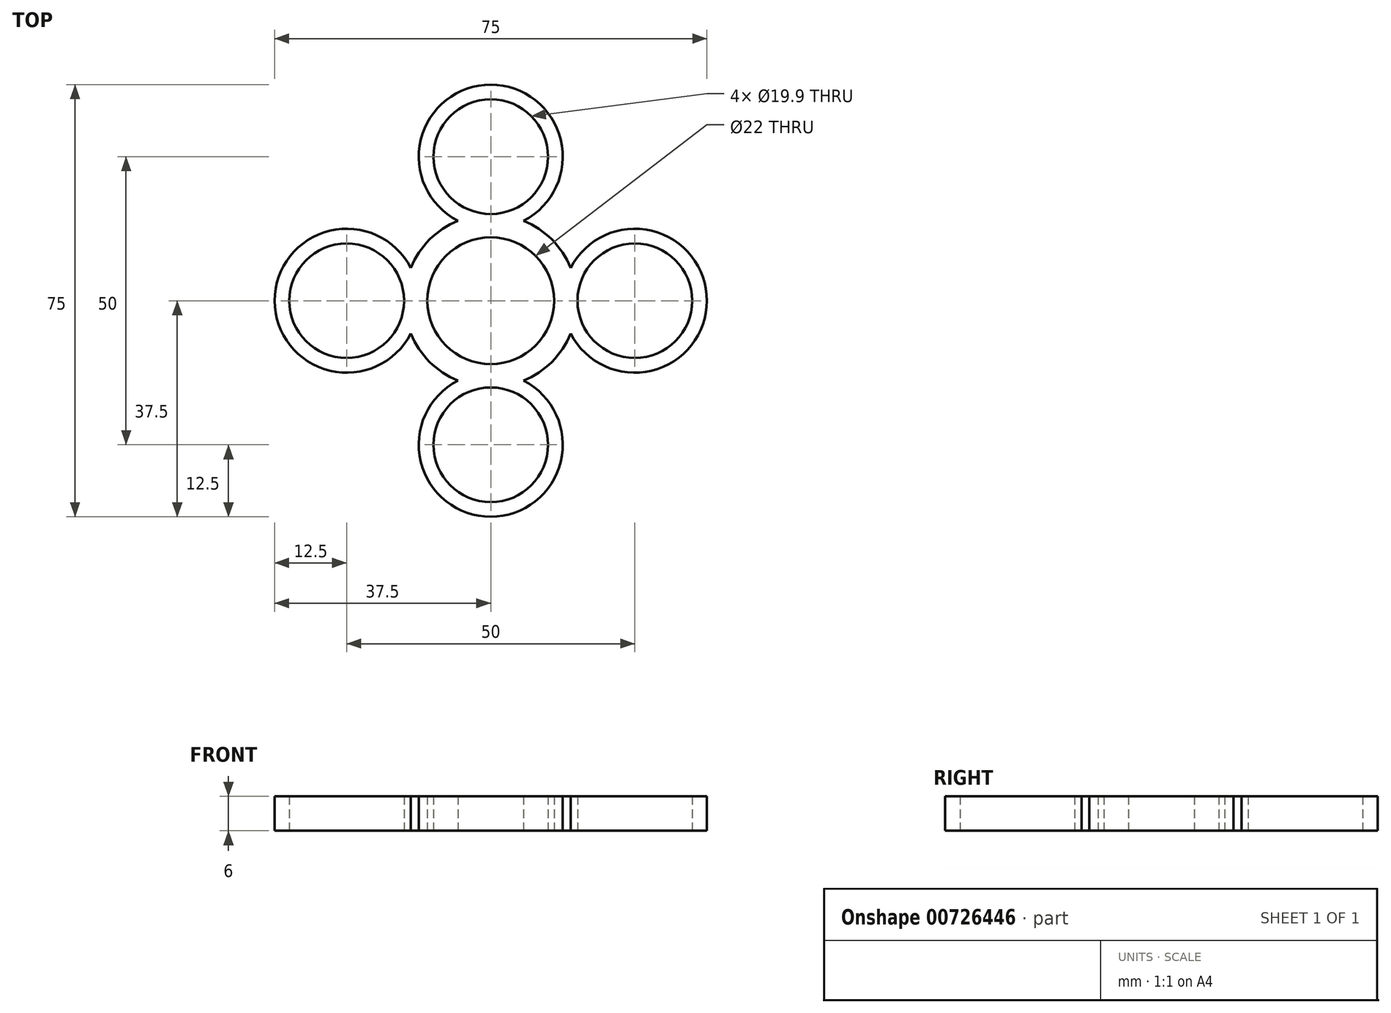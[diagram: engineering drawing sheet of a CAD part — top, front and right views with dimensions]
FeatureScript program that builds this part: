
annotation { "Feature Type Name" : "Feature", "Feature Type Description" : "" }
export const myFeature = defineFeature(function(context is Context, id is Id, definition is map)
    precondition{}
    {
        {
            var Q0;
            Q0=qCreatedBy(makeId("Top.planeOp"),FACE);
            var sketch = newSketch(context, id + "F0", { "sketchPlane" : qUnion([Q0])});
            skArc(sketch, "E0", {"start": v(11, 0) * mm, "mid": v(0, 11) * mm, "end": v(-11, 0) * mm});
            skCircle(sketch, "E1", {"center": v(0, 25) * mm, "radius": 9.95 * mm});
            skArc(sketch, "E2", {"start": v(-5.7, 13.87) * mm, "mid": v(-10.6, 10.6) * mm, "end": v(-13.87, 5.7) * mm});
            skArc(sketch, "E3", {"start": v(5.7, 13.88) * mm, "mid": v(0, 37.5) * mm, "end": v(-5.7, 13.88) * mm});
            skPoint(sketch, "E4.endSnap0", {"position": v(0, -15) * mm});
            skArc(sketch, "E5.trimOffspring", {"start": v(13.87, 5.7) * mm, "mid": v(10.6, 10.6) * mm, "end": v(5.7, 13.87) * mm});
            skPoint(sketch, "E4.end.orphan", {"position": v(0, -27.44) * mm});
            skCircle(sketch, "E6.1.0", {"center": v(-25, 0) * mm, "radius": 9.95 * mm});
            skArc(sketch, "E6.1.1", {"start": v(0, 11) * mm, "mid": v(-11, 0) * mm, "end": v(0, -11) * mm});
            skArc(sketch, "E6.1.2", {"start": v(-5.7, 13.87) * mm, "mid": v(-10.6, 10.6) * mm, "end": v(-13.88, 5.7) * mm});
            skArc(sketch, "E6.1.3", {"start": v(-13.87, -5.7) * mm, "mid": v(-10.6, -10.6) * mm, "end": v(-5.7, -13.87) * mm});
            skArc(sketch, "E6.1.4", {"start": v(-13.88, 5.7) * mm, "mid": v(-37.5, 0) * mm, "end": v(-13.88, -5.7) * mm});
            skCircle(sketch, "E6.2.0", {"center": v(0, -25) * mm, "radius": 9.95 * mm});
            skArc(sketch, "E6.2.1", {"start": v(-11, 0) * mm, "mid": v(0, -11) * mm, "end": v(11, 0) * mm});
            skArc(sketch, "E6.2.2", {"start": v(-13.87, -5.7) * mm, "mid": v(-10.6, -10.6) * mm, "end": v(-5.7, -13.88) * mm});
            skArc(sketch, "E6.2.3", {"start": v(5.7, -13.87) * mm, "mid": v(10.6, -10.6) * mm, "end": v(13.87, -5.7) * mm});
            skArc(sketch, "E6.2.4", {"start": v(-5.7, -13.88) * mm, "mid": v(0, -37.5) * mm, "end": v(5.7, -13.88) * mm});
            skCircle(sketch, "E6.3.0", {"center": v(25, 0) * mm, "radius": 9.95 * mm});
            skArc(sketch, "E6.3.1", {"start": v(0, -11) * mm, "mid": v(11, 0) * mm, "end": v(0, 11) * mm});
            skArc(sketch, "E6.3.2", {"start": v(5.7, -13.87) * mm, "mid": v(10.6, -10.6) * mm, "end": v(13.88, -5.7) * mm});
            skArc(sketch, "E6.3.4", {"start": v(13.88, -5.7) * mm, "mid": v(37.5, 0) * mm, "end": v(13.88, 5.7) * mm});
            skPoint(sketch, "E7.orphan", {"position": v(0, 15) * mm});
            skPoint(sketch, "E8.orphan", {"position": v(15, 0) * mm});
            skPoint(sketch, "E9.orphan", {"position": v(-15, 0) * mm});
            skSolve(sketch);
        }
        {
            var Q0;
            Q0 = qSketchRegion(id + "F0", true);
            extrude(context, id + "F1", {"entities" : qUnion([Q0]), "depth" : 6 * mm, "offsetDistance" : 25 * mm});
        }
    });
